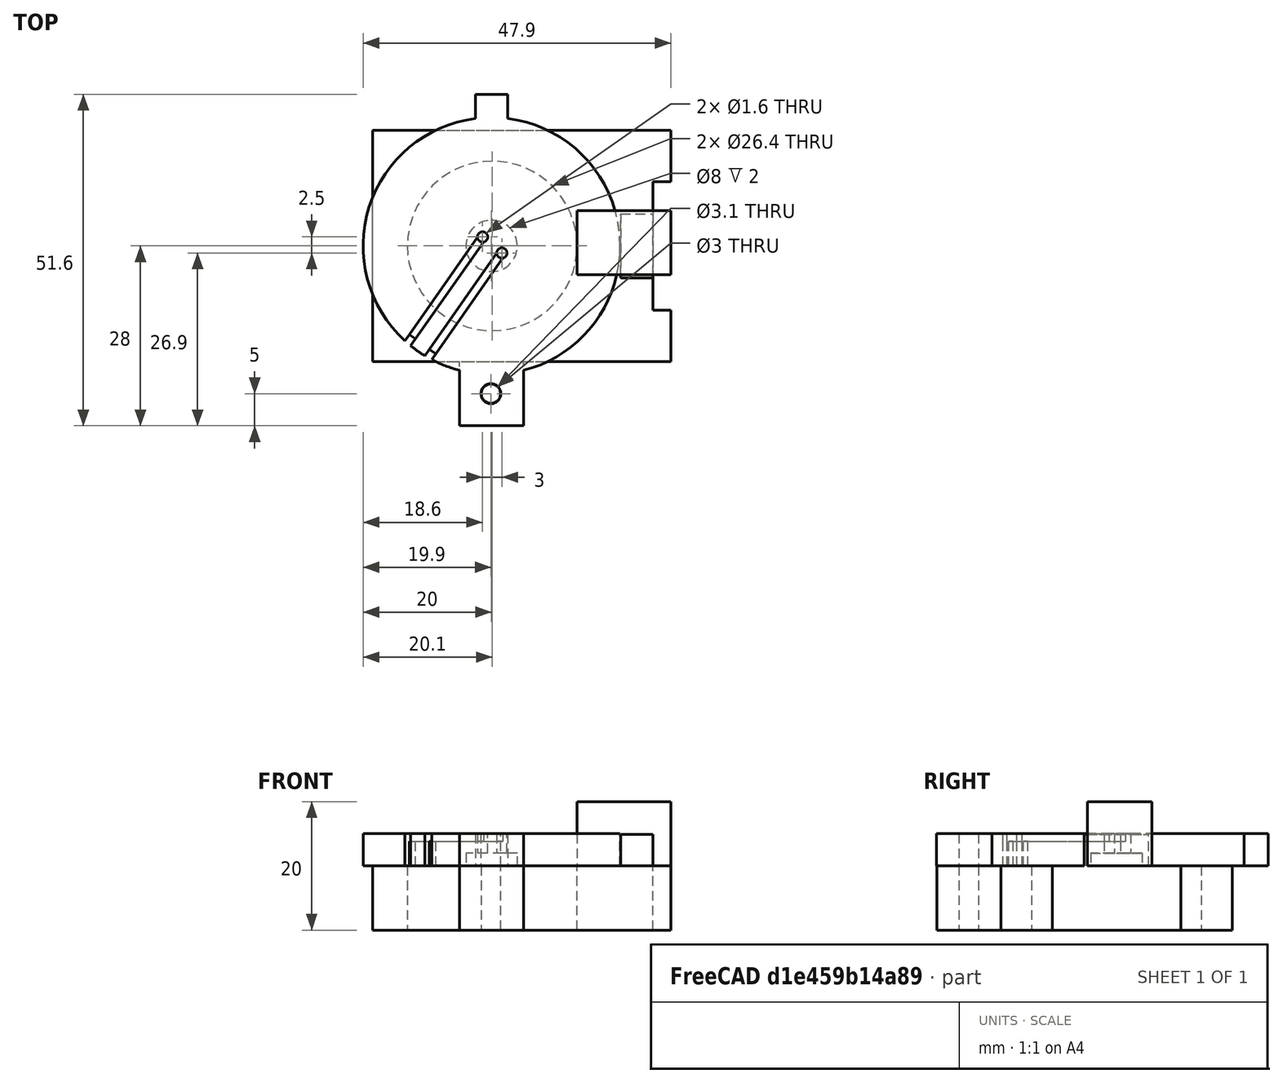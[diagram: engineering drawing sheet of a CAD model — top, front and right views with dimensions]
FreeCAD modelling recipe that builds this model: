
FCSTD DOCUMENT  (FreeCAD 1.0R39319 (Git))
Label: CdSHolderBooleaned1
License: All rights reserved
LicenseURL: https://en.wikipedia.org/wiki/All_rights_reserved
objects: Part::Box×11, Part::Cut×11, Part::Cylinder×7, Part::Fuse×5
note: 34 computed .brp shape members not serialized (recipe doc carries the construction recipe); baked Part::Feature solids carry a one-line shape summary decoded from their .brp

FEATURE [Part::Cylinder] Cylinder  label="cardboardBarrelHolder"
  Angle = 360
  AttacherType = Attacher::AttachEngine3D
  FirstAngle = 0
  Height = 40
  Placement = pos=(-1.1,0,-20) rot=(0,0,1;0rad)
  Radius = 13.2
  SecondAngle = 0
FEATURE [Part::Box] Box  label="mainPiece"
  AttacherType = Attacher::AttachEngine3D
  Height = 46.4
  Length = 10
  Placement = pos=(-19.7,-18,-4.4e-15) rot=(0,1,0;1.5708rad)
  Width = 36
FEATURE [Part::Box] Box001  label="Cube001"
  AttacherType = Attacher::AttachEngine3D
  Height = 14.6
  Length = 10
  Placement = pos=(12.1,-4.5,10) rot=(0,1,0;1.5708rad)
  Width = 10
FEATURE [Part::Box] Box002  label="hingePinTab"
  AttacherType = Attacher::AttachEngine3D
  Height = 10
  Length = 10
  Placement = pos=(-6.2,-27.952,-10) rot=(0,0,1;0rad)
  Width = 10
FEATURE [Part::Cylinder] Cylinder001  label="hingeTabHole"
  Angle = 360
  AttacherType = Attacher::AttachEngine3D
  FirstAngle = 0
  Height = 30
  Placement = pos=(-1.3,-23,-12) rot=(0,0,1;0rad)
  Radius = 1.5
  SecondAngle = 0
FEATURE [Part::Cylinder] Cylinder002  label="shutter"
  Angle = 360
  AttacherType = Attacher::AttachEngine3D
  FirstAngle = 0
  Height = 5
  Placement = pos=(-1.2,0,0) rot=(0,0,1;0rad)
  Radius = 20
  SecondAngle = 0
FEATURE [Part::Box] Box003  label="shutterHingeTab"
  AttacherType = Attacher::AttachEngine3D
  Height = 5
  Length = 10
  Placement = pos=(-6.2,-28,0) rot=(0,0,1;0rad)
  Width = 14
FEATURE [Part::Box] Box004  label="swivelStop"
  AttacherType = Attacher::AttachEngine3D
  Height = 5
  Length = 5
  Placement = pos=(18.9,-5,-0.1) rot=(0,0,1;0rad)
  Width = 10
FEATURE [Part::Box] Box005  label="footCutout"
  AttacherType = Attacher::AttachEngine3D
  Height = 20
  Length = 10
  Placement = pos=(23.9,-10,-18) rot=(0,0,1;0rad)
  Width = 20
FEATURE [Part::Cylinder] Cylinder003  label="shutterTabHole"
  Angle = 360
  AttacherType = Attacher::AttachEngine3D
  FirstAngle = 0
  Height = 50
  Placement = pos=(-1.3,-23,-12) rot=(0,0,1;0rad)
  Radius = 1.55
  SecondAngle = 0
FEATURE [Part::Box] Box006  label="shutterMoveTab"
  AttacherType = Attacher::AttachEngine3D
  Height = 5
  Length = 5
  Placement = pos=(-3.7,18.6,0) rot=(0,0,1;0rad)
  Width = 5
FEATURE [Part::Cylinder] Cylinder004  label="CdSDivot"
  Angle = 360
  AttacherType = Attacher::AttachEngine3D
  FirstAngle = 0
  Height = 10
  Placement = pos=(-1.2,0,-8) rot=(0,0,1;0rad)
  Radius = 4
  SecondAngle = 0
FEATURE [Part::Cylinder] Cylinder005  label="CdSWire1"
  Angle = 360
  AttacherType = Attacher::AttachEngine3D
  FirstAngle = 0
  Height = 30
  Placement = pos=(0.4,-1.1,-18) rot=(0,0,1;0rad)
  Radius = 0.8
  SecondAngle = 0
FEATURE [Part::Cylinder] Cylinder006  label="CdsWire2"
  Angle = 360
  AttacherType = Attacher::AttachEngine3D
  FirstAngle = 0
  Height = 30
  Placement = pos=(-2.6,1.4,-18) rot=(0,0,1;0rad)
  Radius = 0.8
  SecondAngle = 0
FEATURE [Part::Box] Box007  label="radialTransit1"
  AttacherType = Attacher::AttachEngine3D
  Height = 10
  Length = 1.2
  Placement = pos=(-17.353,-25.3595,3.8) rot=(0,0,1;5.67232rad)
  Width = 30
FEATURE [Part::Box] Box008  label="radialTransit2"
  AttacherType = Attacher::AttachEngine3D
  Height = 10
  Length = 1.2
  Placement = pos=(-20.3756,-22.8768,3.8) rot=(0,0,1;5.67232rad)
  Width = 30
FEATURE [Part::Box] Box009  label="radialTransit3"
  AttacherType = Attacher::AttachEngine3D
  Height = 10
  Length = 1.2
  Placement = pos=(-10.8716,-16.103,-4.1) rot=(-0.913318,0.287968,0.287968;4.62184rad)
  Width = 30
FEATURE [Part::Box] Box010  label="radialTransit4"
  AttacherType = Attacher::AttachEngine3D
  Height = 10
  Length = 1.2
  Placement = pos=(-14.0089,-13.7842,-4.1) rot=(-0.913318,0.287968,0.287968;4.62184rad)
  Width = 30
FEATURE [Part::Cut] Cut
  Base = -> Box
  Tool = -> Cylinder
FEATURE [Part::Cut] Cut001  label="mainPiece1"
  Base = -> Cut
  Tool = -> Box005
FEATURE [Part::Cut] Cut002
  Base = -> Cylinder002
  Tool = -> Cylinder004
FEATURE [Part::Cut] Cut003
  Base = -> Cut002
  Tool = -> Cylinder005
FEATURE [Part::Cut] Cut004
  Base = -> Cut003
  Tool = -> Cylinder006
FEATURE [Part::Cut] Cut005
  Base = -> Cut004
  Tool = -> Box007
FEATURE [Part::Cut] Cut006
  Base = -> Cut005
  Tool = -> Box008
FEATURE [Part::Cut] Cut007
  Base = -> Cut006
  Tool = -> Box009
FEATURE [Part::Cut] Cut008  label="shutter1"
  Base = -> Cut007
  Tool = -> Box010
FEATURE [Part::Cut] Cut009  label="shutterHingeTab001"
  Base = -> Box003
  Tool = -> Cylinder003
FEATURE [Part::Cut] Cut010  label="mainPieceHingeTab"
  Base = -> Box002
  Tool = -> Cylinder001
FEATURE [Part::Fuse] Fusion  label="mainPiece2"
  Base = -> Cut001
  Tool = -> Cut010
FEATURE [Part::Fuse] Fusion001  label="shutter2"
  Base = -> Cut008
  Tool = -> Cut009
FEATURE [Part::Fuse] Fusion002  label="Don'tUsemainPiece3"
  Base = -> Cut001
  Tool = -> Box004
FEATURE [Part::Fuse] Fusion003  label="shutter4"
  Base = -> Fusion001
  Tool = -> Box006
FEATURE [Part::Fuse] Fusion004  label="mainPiece10"
  Base = -> Fusion
  Tool = -> Box004
